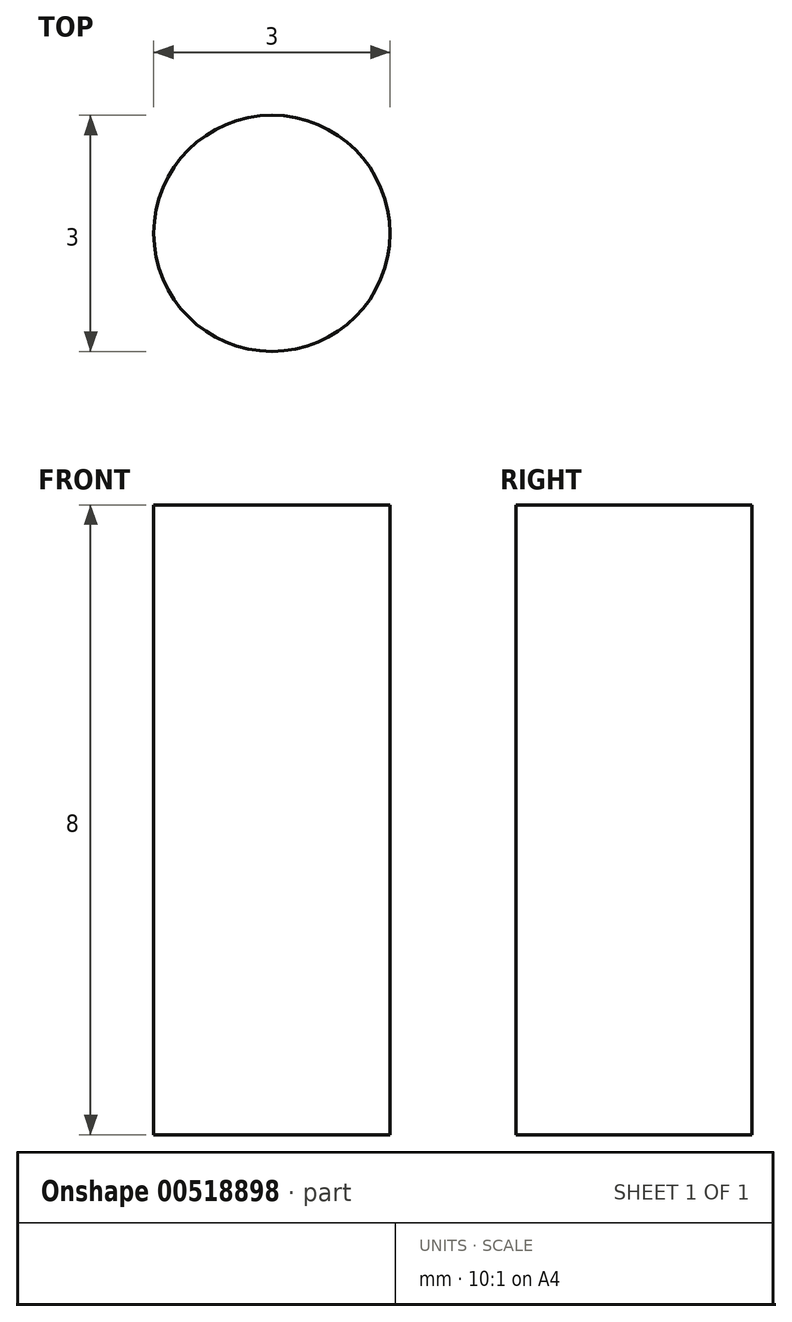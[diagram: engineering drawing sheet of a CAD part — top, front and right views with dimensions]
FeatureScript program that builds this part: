
annotation { "Feature Type Name" : "Feature", "Feature Type Description" : "" }
export const myFeature = defineFeature(function(context is Context, id is Id, definition is map)
    precondition{}
    {
        {
            var Q0;
            Q0=qCreatedBy(makeId("Top.planeOp"),FACE);
            var sketch = newSketch(context, id + "F0", { "sketchPlane" : qUnion([Q0])});
            skCircle(sketch, "E0", {"center": v(0, 0) * mm, "radius": 1.5 * mm});
            skSolve(sketch);
        }
        {
            var Q0;
            Q0=makeQuery(id+"F0.imprint","IMPRINT",FACE,{"disambiguationData":[TD([[makeQuery(id+"F0.imprint","IMPRINT",EDGE,{"derivedFrom":sQuery(id+"F0.wireOp",EDGE,"E0")}),1.0]])]});
            extrude(context, id + "F1", {"entities" : qUnion([Q0]), "depth" : 8 * mm, "offsetDistance" : 25 * mm});
        }
    });
